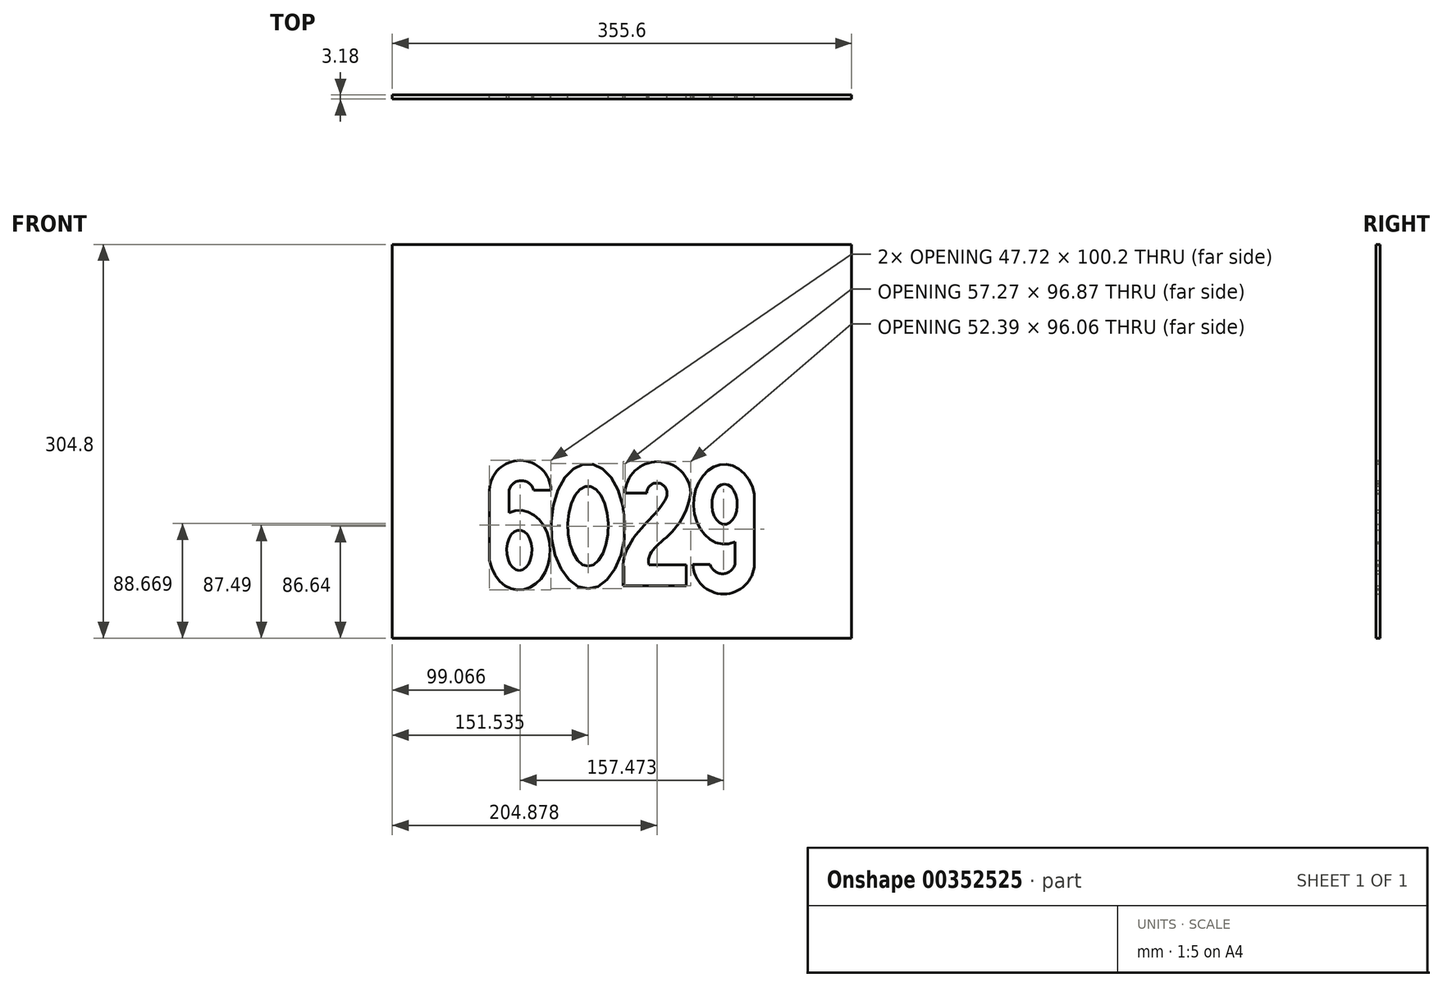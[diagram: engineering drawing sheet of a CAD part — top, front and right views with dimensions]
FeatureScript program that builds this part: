
annotation { "Feature Type Name" : "Feature", "Feature Type Description" : "" }
export const myFeature = defineFeature(function(context is Context, id is Id, definition is map)
    precondition{}
    {
        {
            var Q0;
            Q0=qCreatedBy(makeId("Front.planeOp"),FACE);
            var sketch = newSketch(context, id + "F0", { "sketchPlane" : qUnion([Q0])});
            skLineSegment(sketch, "E0", {"start": v(-95.03, -29.54) * mm, "end": v(-108.48, -29.54) * mm});
            skArc(sketch, "E1", {"start": v(-108.48, -29.54) * mm, "mid": v(-118.05, -22.2) * mm, "end": v(-127.62, -29.54) * mm});
            skArc(sketch, "E2", {"start": v(-95.03, -29.54) * mm, "mid": v(-118.9, -6.52) * mm, "end": v(-142.76, -29.54) * mm});
            skLineSegment(sketch, "E3", {"start": v(-142.76, -29.54) * mm, "end": v(-142.76, -83.99) * mm});
            skLineSegment(sketch, "E4", {"start": v(-127.62, -29.54) * mm, "end": v(-127.62, -46.95) * mm});
            skEllipse(sketch, "E5", {"center": v(-119.6, -76.04) * mm, "majorRadius": 15.63 * mm, "minorRadius": 9.82 * mm, "majorAxis": v(0, -1)});
            skEllipticalArc(sketch, "E6", {});
            skEllipse(sketch, "E7", {"center": v(-66.42, -57.47) * mm, "majorRadius": 48.44 * mm, "minorRadius": 28.64 * mm, "majorAxis": v(0, -1)});
            skEllipse(sketch, "E8", {"center": v(-66.42, -57.47) * mm, "majorRadius": 30.97 * mm, "minorRadius": 15.64 * mm, "majorAxis": v(0, -1)});
            skLineSegment(sketch, "E9", {"start": v(-20.92, -31.85) * mm, "end": v(-37.78, -31.85) * mm});
            skLineSegment(sketch, "E10", {"start": v(9.67, -103.47) * mm, "end": v(-39.28, -103.47) * mm});
            skLineSegment(sketch, "E11", {"start": v(9.67, -103.47) * mm, "end": v(9.67, -87.41) * mm});
            skLineSegment(sketch, "E12", {"start": v(9.67, -87.41) * mm, "end": v(-19.4, -87.41) * mm});
            skArc(sketch, "E13", {"start": v(13.11, -31.85) * mm, "mid": v(-12.34, -7.4) * mm, "end": v(-37.78, -31.85) * mm});
            skFitSpline(sketch, "E14", {"points": [v(13.11, -31.85) * mm, v(-19.4, -87.41) * mm], "startDerivative": vector(-19.5, -113.57) * mm, "endDerivative": vector(9.18, -55.06) * mm});
            skArc(sketch, "E15", {"start": v(-5.24, -31.85) * mm, "mid": v(-13.08, -24.01) * mm, "end": v(-20.92, -31.85) * mm});
            skLineSegment(sketch, "E16", {"start": v(-39.28, -87.41) * mm, "end": v(-39.28, -103.47) * mm});
            skPoint(sketch, "E16.startSnap0", {"position": v(-4.86, -87.41) * mm});
            skFitSpline(sketch, "E17", {"points": [v(-39.28, -87.41) * mm, v(-5.24, -31.85) * mm], "startDerivative": vector(4, 74.7) * mm, "endDerivative": vector(1.15, 42.45) * mm});
            skLineSegment(sketch, "E18", {"start": v(14.72, -86.95) * mm, "end": v(28.17, -86.95) * mm});
            skArc(sketch, "E19", {"start": v(28.17, -86.95) * mm, "mid": v(37.73, -94.28) * mm, "end": v(47.3, -86.95) * mm});
            skArc(sketch, "E20", {"start": v(14.72, -86.95) * mm, "mid": v(38.58, -109.97) * mm, "end": v(62.44, -86.95) * mm});
            skLineSegment(sketch, "E21", {"start": v(62.44, -86.95) * mm, "end": v(62.44, -32.5) * mm});
            skEllipse(sketch, "E22", {"center": v(39.29, -40.45) * mm, "majorRadius": 15.63 * mm, "minorRadius": 9.82 * mm, "majorAxis": v(0, 1)});
            skEllipticalArc(sketch, "E23", {});
            skLineSegment(sketch, "E24", {"start": v(47.3, -86.95) * mm, "end": v(47.3, -69.54) * mm});
            skLineSegment(sketch, "E25.bottom", {"start": v(-217.96, -144.11) * mm, "end": v(137.64, -144.11) * mm});
            skLineSegment(sketch, "E25.top", {"start": v(-217.96, 160.69) * mm, "end": v(137.64, 160.69) * mm});
            skLineSegment(sketch, "E25.left", {"start": v(-217.96, -144.11) * mm, "end": v(-217.96, 160.69) * mm});
            skLineSegment(sketch, "E25.right", {"start": v(137.64, -144.11) * mm, "end": v(137.64, 160.69) * mm});
            const initialGuessF0  = {"E6": [-0.11960215085978274, -0.07604163817507714, 0, -1, 0.030871672671253313, 0.023960798996810216, 4.972696766627012, 3.4826250035732884], "E23": [0.039287207804596644, -0.04044740727788268, 0, 1, 0.030871672671253313, 0.023960798996810216, 4.972696766627028, 3.482625003573289]};
            skSetInitialGuess(sketch, initialGuessF0);
            skSolve(sketch);
        }
        {
            var Q0;
            Q0=makeQuery(id+"F0.imprint","IMPRINT",FACE,{"disambiguationData":[TD([[makeQuery(id+"F0.imprint","IMPRINT",EDGE,{"derivedFrom":sQuery(id+"F0.wireOp",EDGE,"E0")}),1.0]])]});
            var Q1;
            Q1=makeQuery(id+"F0.imprint","IMPRINT",FACE,{"disambiguationData":[TD([[makeQuery(id+"F0.imprint","IMPRINT",EDGE,{"derivedFrom":sQuery(id+"F0.wireOp",EDGE,"E8")}),1.0]])]});
            var Q2;
            Q2=makeQuery(id+"F0.imprint","IMPRINT",FACE,{"disambiguationData":[TD([[makeQuery(id+"F0.imprint","IMPRINT",EDGE,{"derivedFrom":sQuery(id+"F0.wireOp",EDGE,"E5")}),1.0]])]});
            var Q3;
            Q3=makeQuery(id+"F0.imprint","IMPRINT",FACE,{"disambiguationData":[TD([[makeQuery(id+"F0.imprint","IMPRINT",EDGE,{"derivedFrom":sQuery(id+"F0.wireOp",EDGE,"E22")}),1.0]])]});
            extrude(context, id + "F1", {"entities" : qUnion([Q0, Q1, Q2, Q3]), "depth" : 3.17 * mm});
        }
    });
